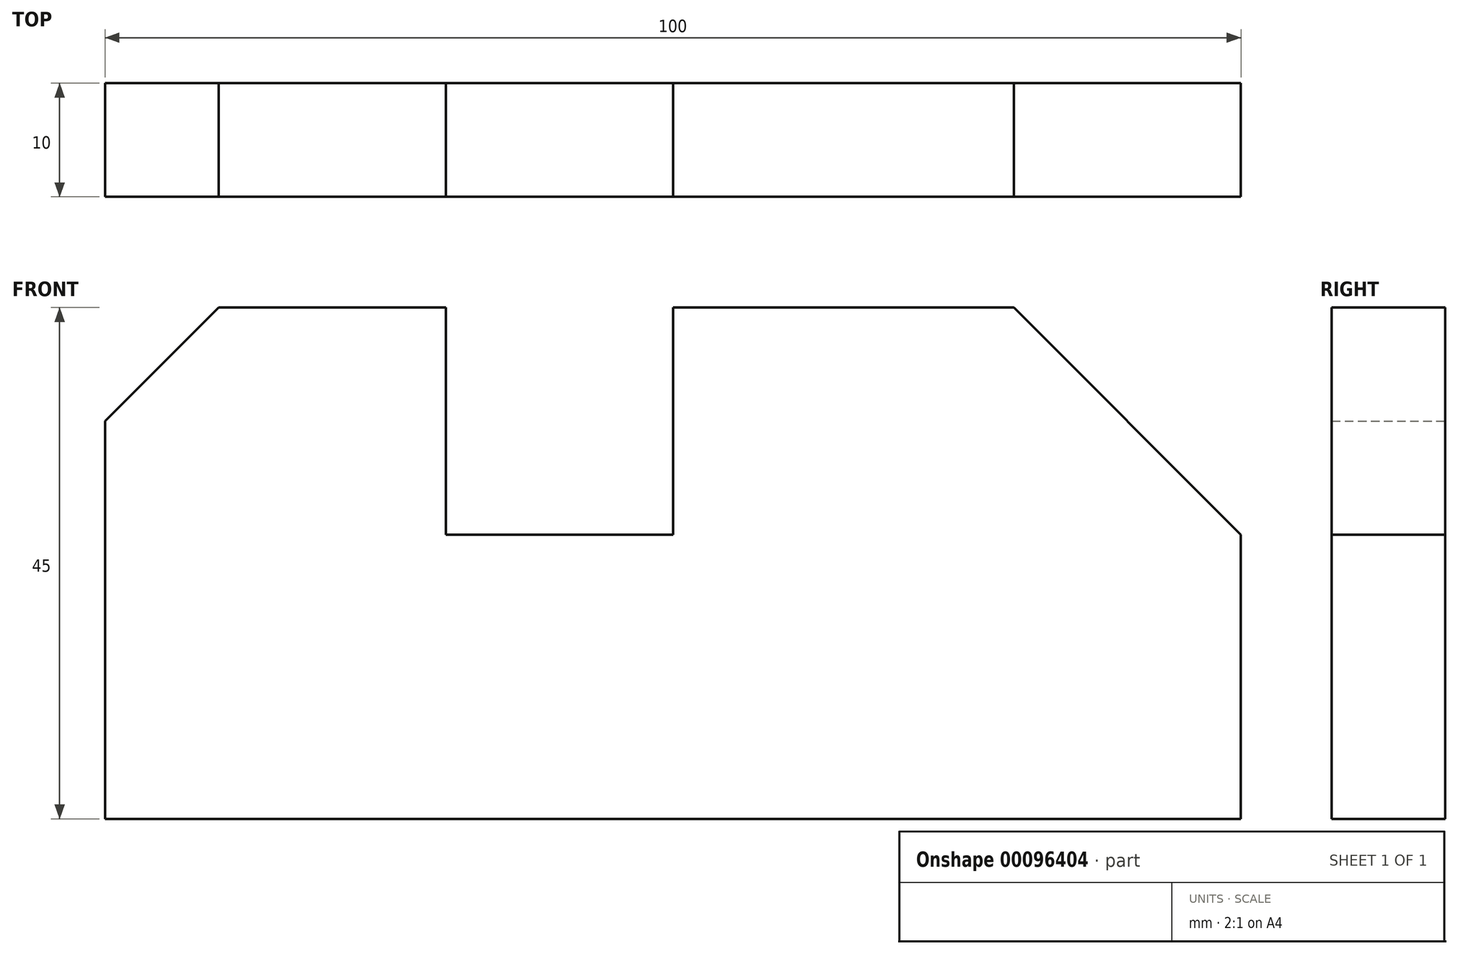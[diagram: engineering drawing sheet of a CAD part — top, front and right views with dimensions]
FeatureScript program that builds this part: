
annotation { "Feature Type Name" : "Feature", "Feature Type Description" : "" }
export const myFeature = defineFeature(function(context is Context, id is Id, definition is map)
    precondition{}
    {
        {
            var Q0;
            Q0=qCreatedBy(makeId("Front.planeOp"),FACE);
            var sketch = newSketch(context, id + "F0", { "sketchPlane" : qUnion([Q0])});
            skLineSegment(sketch, "E0", {"start": v(-5.1, 0) * mm, "end": v(94.9, 0) * mm});
            skLineSegment(sketch, "E1", {"start": v(94.9, 0) * mm, "end": v(94.9, 25) * mm});
            skLineSegment(sketch, "E2", {"start": v(94.9, 25) * mm, "end": v(74.9, 45) * mm});
            skLineSegment(sketch, "E3", {"start": v(74.9, 45) * mm, "end": v(44.9, 45) * mm});
            skLineSegment(sketch, "E4", {"start": v(44.9, 45) * mm, "end": v(44.9, 25) * mm});
            skLineSegment(sketch, "E5", {"start": v(44.9, 25) * mm, "end": v(24.9, 25) * mm});
            skLineSegment(sketch, "E6", {"start": v(24.9, 25) * mm, "end": v(24.9, 45) * mm});
            skLineSegment(sketch, "E7", {"start": v(24.9, 45) * mm, "end": v(4.9, 45) * mm});
            skLineSegment(sketch, "E8", {"start": v(-5.1, 0) * mm, "end": v(-5.1, 35) * mm});
            skLineSegment(sketch, "E9", {"start": v(-5.1, 35) * mm, "end": v(4.9, 45) * mm});
            skSolve(sketch);
        }
        {
            var Q0;
            Q0 = qSketchRegion(id + "F0", true);
            extrude(context, id + "F1", {"entities" : qUnion([Q0]), "depth" : 10 * mm});
        }
    });
